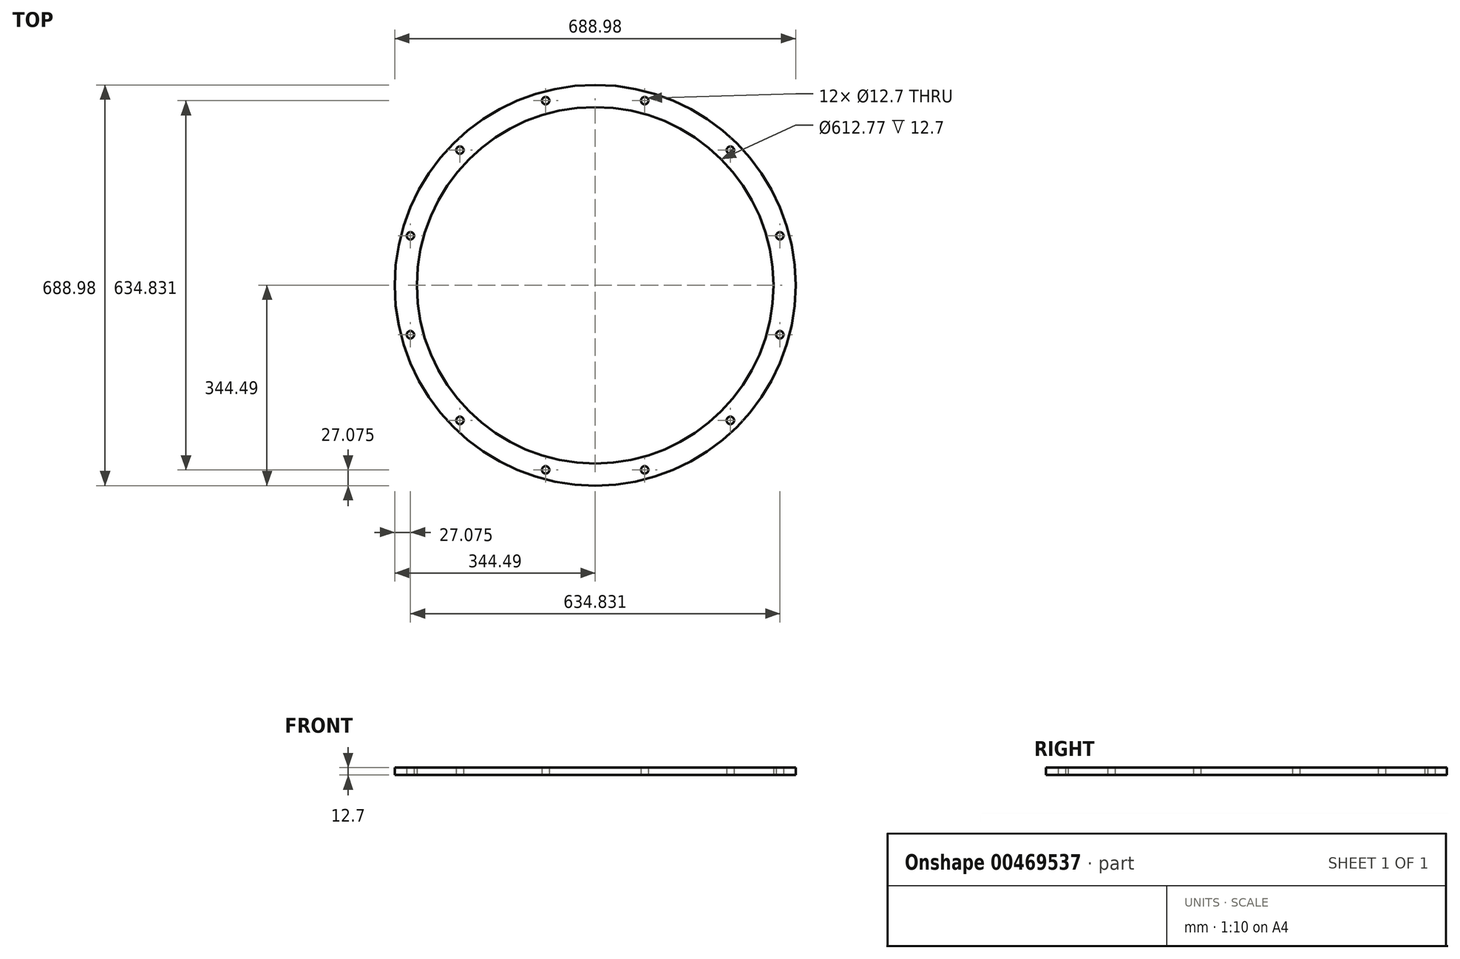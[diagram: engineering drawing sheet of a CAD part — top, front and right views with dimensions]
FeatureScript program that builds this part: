
annotation { "Feature Type Name" : "Feature", "Feature Type Description" : "" }
export const myFeature = defineFeature(function(context is Context, id is Id, definition is map)
    precondition{}
    {
        {
            var Q0;
            Q0=qCreatedBy(makeId("Top.planeOp"),FACE);
            var sketch = newSketch(context, id + "F0", { "sketchPlane" : qUnion([Q0])});
            skCircle(sketch, "E0", {"center": v(0, 0) * mm, "radius": 344.49 * mm});
            skCircle(sketch, "E1", {"center": v(0, 0) * mm, "radius": 306.39 * mm});
            skCircle(sketch, "E2", {"center": v(0, 0) * mm, "radius": 328.61 * mm, "construction": true});
            skCircle(sketch, "E3", {"center": v(317.42, 85.05) * mm, "radius": 6.35 * mm});
            skLineSegment(sketch, "E4", {"start": v(0, 0) * mm, "end": v(317.42, 85.05) * mm, "construction": true});
            skCircle(sketch, "E5.1.0", {"center": v(232.36, 232.36) * mm, "radius": 6.35 * mm});
            skCircle(sketch, "E5.2.0", {"center": v(85.05, 317.42) * mm, "radius": 6.35 * mm});
            skCircle(sketch, "E5.3.0", {"center": v(-85.05, 317.42) * mm, "radius": 6.35 * mm});
            skCircle(sketch, "E5.4.0", {"center": v(-232.36, 232.36) * mm, "radius": 6.35 * mm});
            skCircle(sketch, "E5.5.0", {"center": v(-317.42, 85.05) * mm, "radius": 6.35 * mm});
            skCircle(sketch, "E5.6.0", {"center": v(-317.42, -85.05) * mm, "radius": 6.35 * mm});
            skCircle(sketch, "E5.7.0", {"center": v(-232.36, -232.36) * mm, "radius": 6.35 * mm});
            skCircle(sketch, "E5.8.0", {"center": v(-85.05, -317.42) * mm, "radius": 6.35 * mm});
            skCircle(sketch, "E5.9.0", {"center": v(85.05, -317.42) * mm, "radius": 6.35 * mm});
            skCircle(sketch, "E5.10.0", {"center": v(232.36, -232.36) * mm, "radius": 6.35 * mm});
            skCircle(sketch, "E5.11.0", {"center": v(317.42, -85.05) * mm, "radius": 6.35 * mm});
            skLineSegment(sketch, "E6", {"start": v(0, 0) * mm, "end": v(317.42, -85.05) * mm, "construction": true});
            skSolve(sketch);
        }
        {
            var Q0;
            Q0 = qSketchRegion(id + "F0", true);
            extrude(context, id + "F1", {"entities" : qUnion([Q0]), "depth" : 12.7 * mm, "offsetDistance" : 25.4 * mm});
        }
    });
